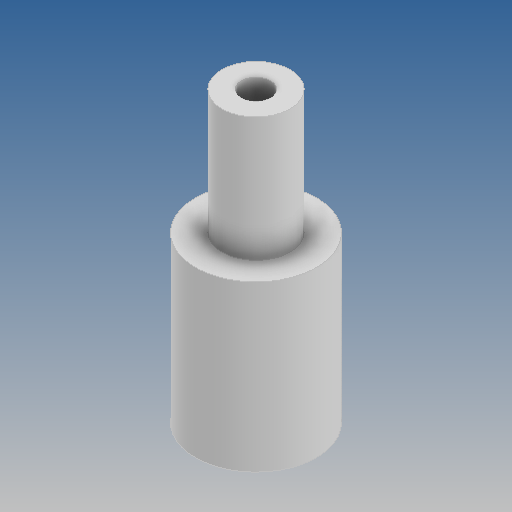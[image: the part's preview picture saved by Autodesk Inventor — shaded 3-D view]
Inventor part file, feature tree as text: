
AUTODESK INVENTOR PART (.ipt)
format: ipt  version: 2020 (Build 240168000, 168)  size: 113,664 bytes
history: native  units: mm
features: revolve x1, sketch x1
ambient origin geometry x8: Origin, YZ Plane, XZ Plane, XY Plane, X Axis, Y Axis, Z Axis, Center Point
bodies: Solid1 (feature_tree)
feature tree (2):
  revolve  "Revolution1"  [1 undecoded]
  sketch  "Sketch1"  dims[d0=3.35mm d1=13.4mm d2=1.57mm d3=1.57mm d4=1.2mm d5=1.57mm d7=23.5mm d8=90.0deg]
note: 1 required parameter value undecoded (feature->parameter linkage not recoverable at this tier; creation-order binding heuristic only, values carry confidence <= 0.55)
